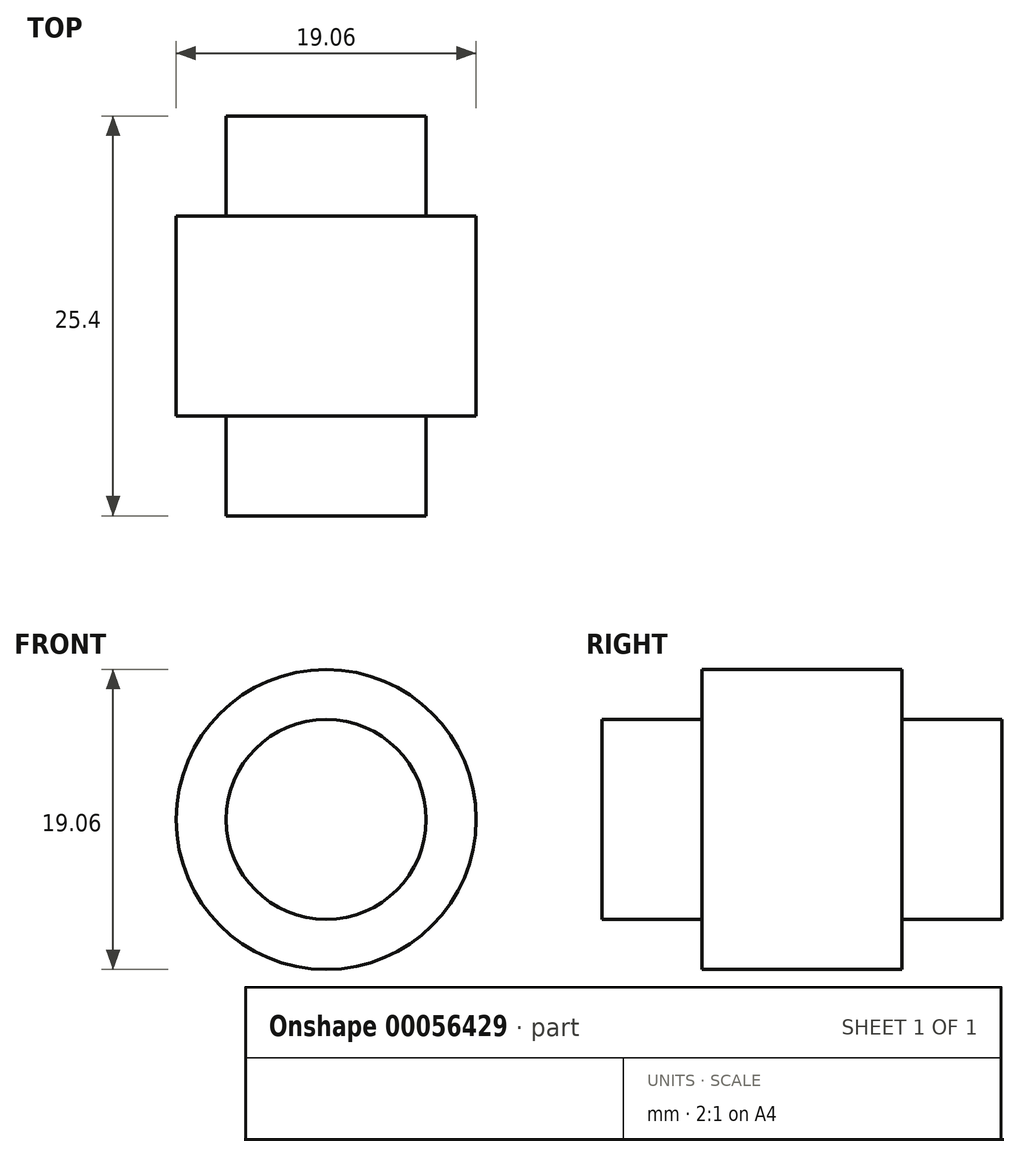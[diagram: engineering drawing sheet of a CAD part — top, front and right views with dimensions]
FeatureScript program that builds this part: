
annotation { "Feature Type Name" : "Feature", "Feature Type Description" : "" }
export const myFeature = defineFeature(function(context is Context, id is Id, definition is map)
    precondition{}
    {
        {
            var Q0;
            Q0=qCreatedBy(makeId("Front.planeOp"),FACE);
            var sketch = newSketch(context, id + "F0", { "sketchPlane" : qUnion([Q0])});
            skCircle(sketch, "E0", {"center": v(0, 0) * mm, "radius": 6.35 * mm});
            skCircle(sketch, "E1", {"center": v(0, 0) * mm, "radius": 9.53 * mm});
            skSolve(sketch);
        }
        {
            var Q0;
            Q0=makeQuery(id+"F0.imprint","IMPRINT",FACE,{"disambiguationData":[TD([[makeQuery(id+"F0.imprint","IMPRINT",EDGE,{"derivedFrom":sQuery(id+"F0.wireOp",EDGE,"E0")}),1.0]])]});
            extrude(context, id + "F1", {"entities" : qUnion([Q0]), "endBound" : BoundingType.SYMMETRIC, "depth" : 25.4 * mm});
        }
        {
            var Q0;
            Q0=qSketchRegion(id+"F0",true);
            extrude(context, id + "F2", {"entities" : qUnion([Q0]), "operationType" : NewBodyOperationType.ADD, "endBound" : BoundingType.SYMMETRIC, "depth" : 12.7 * mm});
        }
    });
